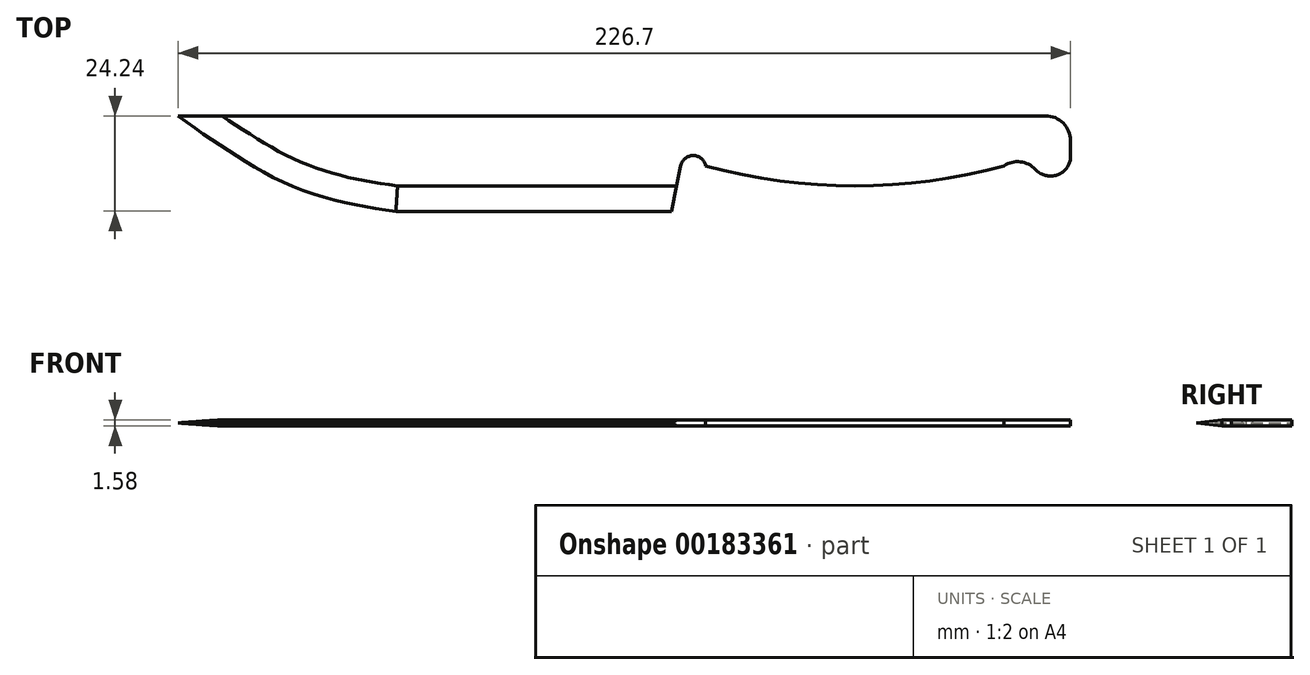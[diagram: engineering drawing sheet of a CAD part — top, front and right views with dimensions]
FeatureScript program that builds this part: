
annotation { "Feature Type Name" : "Feature", "Feature Type Description" : "" }
export const myFeature = defineFeature(function(context is Context, id is Id, definition is map)
    precondition{}
    {
        {
            var Q0;
            Q0=qCreatedBy(makeId("Top.planeOp"),FACE);
            var sketch = newSketch(context, id + "F0", { "sketchPlane" : qUnion([Q0])});
            skPoint(sketch, "E0", {"position": v(0, 0) * mm});
            skLineSegment(sketch, "E1.bottom", {"start": v(114.3, 12.7) * mm, "end": v(-114.3, 12.7) * mm, "construction": true});
            skLineSegment(sketch, "E1.top", {"start": v(114.3, -12.7) * mm, "end": v(-114.3, -12.7) * mm, "construction": true});
            skLineSegment(sketch, "E1.left", {"start": v(114.3, 6.35) * mm, "end": v(114.3, -12.7) * mm, "construction": true});
            skLineSegment(sketch, "E1.right", {"start": v(-114.3, 12.7) * mm, "end": v(-114.3, -12.7) * mm, "construction": true});
            skPoint(sketch, "E2", {"position": v(12.7, -12.7) * mm});
            skPoint(sketch, "E3", {"position": v(-114.3, -12.7) * mm});
            skPoint(sketch, "E4", {"position": v(-114.3, 12.7) * mm});
            skPoint(sketch, "E5", {"position": v(114.3, 12.7) * mm});
            skPoint(sketch, "E6", {"position": v(114.3, -12.7) * mm});
            skPoint(sketch, "E7", {"position": v(-57.15, -12.7) * mm});
            skLineSegment(sketch, "E8", {"start": v(-57.15, -12.7) * mm, "end": v(12.7, -12.7) * mm});
            skFitSpline(sketch, "E9", {"points": [v(-57.15, -12.7) * mm, v(-74.56, -9.42) * mm, v(-87.24, -4.72) * mm, v(-95.67, 0) * mm, v(-114.3, 12.7) * mm], "startDerivative": vector(-62.66, 7.42) * mm, "endDerivative": vector(-66.08, 51.33) * mm});
            skLineSegment(sketch, "E10", {"start": v(-114.3, 12.7) * mm, "end": v(107.95, 12.7) * mm});
            skLineSegment(sketch, "E11", {"start": v(114.3, 12.7) * mm, "end": v(114.3, 2.46) * mm});
            skPoint(sketch, "E12", {"position": v(15.24, 0) * mm});
            skPoint(sketch, "E13", {"position": v(21.59, 0) * mm});
            skLineSegment(sketch, "E14", {"start": v(15.24, 0) * mm, "end": v(12.7, -12.7) * mm});
            skArc(sketch, "E15", {"start": v(21.59, 0) * mm, "mid": v(18.41, 2.6) * mm, "end": v(15.24, 0) * mm});
            skPoint(sketch, "E16", {"position": v(101.6, 1) * mm});
            skLineSegment(sketch, "E17", {"start": v(106.5, -1.84) * mm, "end": v(106.68, -1.94) * mm});
            skPoint(sketch, "E18", {"position": v(97.4, 0) * mm});
            skPoint(sketch, "E19", {"position": v(58.42, -12.7) * mm});
            skPoint(sketch, "E20", {"position": v(58.42, -5.08) * mm});
            skArc(sketch, "E21", {"start": v(21.6, 0) * mm, "mid": v(59.5, -5.08) * mm, "end": v(97.4, 0) * mm});
            skArc(sketch, "E22", {"start": v(105.33, -0.91) * mm, "mid": v(101.53, 1) * mm, "end": v(97.4, 0) * mm});
            skArc(sketch, "E23.filletArc", {"start": v(105.33, -0.91) * mm, "mid": v(105.88, -1.42) * mm, "end": v(106.5, -1.84) * mm});
            skPoint(sketch, "E24.visualSharp", {"position": v(114.3, -6.35) * mm});
            skArc(sketch, "E24.filletArc", {"start": v(106.68, -1.94) * mm, "mid": v(111.76, -1.94) * mm, "end": v(114.3, 2.46) * mm});
            skArc(sketch, "E25.filletArc", {"start": v(114.3, 6.35) * mm, "mid": v(112.44, 10.84) * mm, "end": v(107.95, 12.7) * mm});
            skPoint(sketch, "E26", {"position": v(-114.3, 0) * mm});
            skPoint(sketch, "E27", {"position": v(-101.6, 12.7) * mm});
            skPoint(sketch, "E28", {"position": v(-88.9, 12.7) * mm});
            skPoint(sketch, "E29", {"position": v(-101.6, 3.75) * mm});
            skPoint(sketch, "E30", {"position": v(-88.9, -3.9) * mm});
            skPoint(sketch, "E31", {"position": v(-76.2, 12.7) * mm});
            skPoint(sketch, "E32", {"position": v(-63.5, 12.7) * mm});
            skPoint(sketch, "E33", {"position": v(-57.15, 12.7) * mm});
            skPoint(sketch, "E34", {"position": v(-76.2, -8.95) * mm});
            skPoint(sketch, "E35", {"position": v(-63.5, -11.8) * mm});
            skLineSegment(sketch, "E36", {"start": v(-101.6, 3.75) * mm, "end": v(-101.6, 12.7) * mm, "construction": true});
            skLineSegment(sketch, "E37", {"start": v(-88.9, 12.7) * mm, "end": v(-88.9, -3.9) * mm, "construction": true});
            skLineSegment(sketch, "E38", {"start": v(-76.2, 12.7) * mm, "end": v(-76.2, -8.95) * mm, "construction": true});
            skLineSegment(sketch, "E39", {"start": v(-63.5, 12.7) * mm, "end": v(-63.5, -11.8) * mm, "construction": true});
            skLineSegment(sketch, "E40", {"start": v(-57.15, 12.7) * mm, "end": v(-57.15, -12.7) * mm, "construction": true});
            skPoint(sketch, "E41", {"position": v(12.7, 12.7) * mm});
            skPoint(sketch, "E42", {"position": v(15.24, 12.7) * mm});
            skPoint(sketch, "E43", {"position": v(18.41, 2.6) * mm});
            skPoint(sketch, "E44", {"position": v(18.41, 0) * mm});
            skPoint(sketch, "E45", {"position": v(21.59, 12.7) * mm});
            skPoint(sketch, "E46", {"position": v(58.42, 12.7) * mm});
            skPoint(sketch, "E47", {"position": v(97.4, 12.7) * mm});
            skSolve(sketch);
        }
        {
            var Q0;
            Q0=makeQuery(id+"F0.imprint","IMPRINT",FACE,{"disambiguationData":[TD([[makeQuery(id+"F0.imprint","IMPRINT",EDGE,{"derivedFrom":sQuery(id+"F0.wireOp",EDGE,"E8")}),1.0]])]});
            extrude(context, id + "F1", {"entities" : qUnion([Q0]), "endBound" : BoundingType.SYMMETRIC, "depth" : 1.59 * mm});
        }
        {
            var Q0;
            Q0=makeQuery(id+"F1.opExtrude","CAP_EDGE",EDGE,{"disambiguationData":[OSD([sQuery(id+"F0.wireOp",EDGE,"E9")])],"isStart":true});
            var Q1;
            Q1=makeQuery(id+"F1.opExtrude","CAP_EDGE",EDGE,{"disambiguationData":[OSD([sQuery(id+"F0.wireOp",EDGE,"E8")])],"isStart":true});
            chamfer(context, id + "F2", {"entities" : qUnion([Q0, Q1]), "chamferType" : ChamferType.OFFSET_ANGLE, "width" : 7.62 * mm, "oppositeDirection" : false, "angle" : 7 * degree, "tangentPropagation" : true});
        }
        {
            var Q0;
            Q0=makeQuery(id+"F1.opExtrude","CAP_EDGE",EDGE,{"disambiguationData":[OSD([sQuery(id+"F0.wireOp",EDGE,"E8")])],"isStart":false});
            var Q1;
            Q1=makeQuery(id+"F1.opExtrude","CAP_EDGE",EDGE,{"disambiguationData":[OSD([sQuery(id+"F0.wireOp",EDGE,"E9")])],"isStart":false});
            chamfer(context, id + "F3", {"entities" : qUnion([Q0, Q1]), "chamferType" : ChamferType.OFFSET_ANGLE, "width" : 7.62 * mm, "oppositeDirection" : false, "angle" : 7 * degree, "tangentPropagation" : true});
        }
    });
